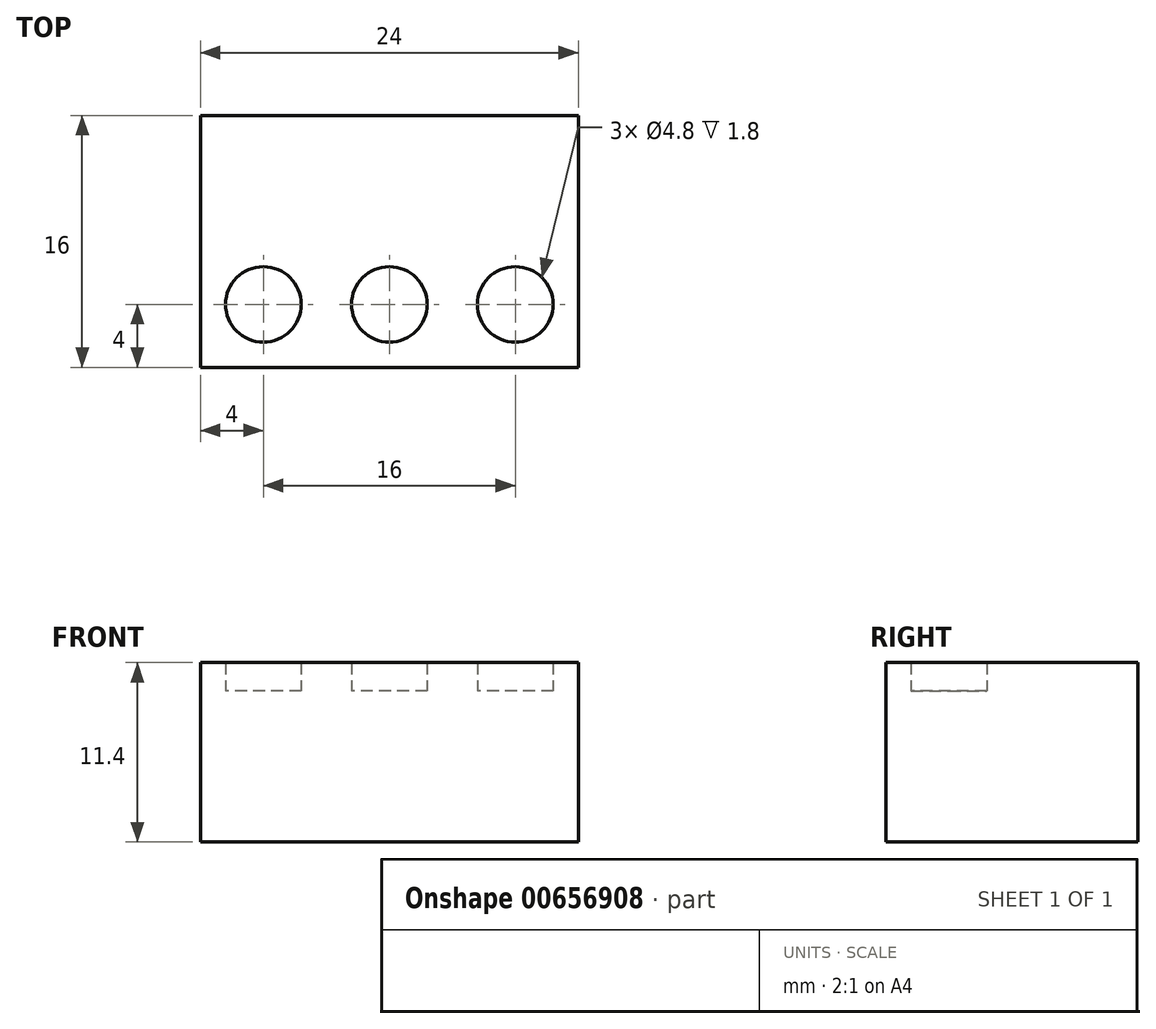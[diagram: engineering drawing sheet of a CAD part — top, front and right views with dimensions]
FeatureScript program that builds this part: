
annotation { "Feature Type Name" : "Feature", "Feature Type Description" : "" }
export const myFeature = defineFeature(function(context is Context, id is Id, definition is map)
    precondition{}
    {
        {
            var Q0;
            Q0=qCreatedBy(makeId("Top.planeOp"),FACE);
            var sketch = newSketch(context, id + "F0", { "sketchPlane" : qUnion([Q0])});
            skLineSegment(sketch, "E0.bottom", {"start": v(0, 0) * mm, "end": v(-24, 0) * mm});
            skLineSegment(sketch, "E0.top", {"start": v(0, 16) * mm, "end": v(-24, 16) * mm});
            skLineSegment(sketch, "E0.left", {"start": v(0, 0) * mm, "end": v(0, 16) * mm});
            skLineSegment(sketch, "E0.right", {"start": v(-24, 0) * mm, "end": v(-24, 16) * mm});
            skSolve(sketch);
        }
        {
            var Q0;
            Q0=makeQuery(id+"F0.imprint","IMPRINT",FACE,{"disambiguationData":[TD([[makeQuery(id+"F0.imprint","IMPRINT",EDGE,{"derivedFrom":sQuery(id+"F0.wireOp",EDGE,"E0.bottom")}),-1.0]])]});
            extrude(context, id + "F1", {"entities" : qUnion([Q0]), "depth" : 9.6 * mm, "offsetDistance" : 25.4 * mm});
        }
        {
            var Q0;
            Q0=makeQuery(id+"F1.opExtrude","CAP_FACE",FACE,{"disambiguationData":[OSD([sQuery(id+"F0.wireOp",EDGE,"E0.bottom"),sQuery(id+"F0.wireOp",EDGE,"E0.top"),sQuery(id+"F0.wireOp",EDGE,"E0.left"),sQuery(id+"F0.wireOp",EDGE,"E0.right")])],"isStart":false});
            var sketch = newSketch(context, id + "F2", { "sketchPlane" : qUnion([Q0])});
            skLineSegment(sketch, "E1", {"start": v(-24, 8) * mm, "end": v(0, 8) * mm, "construction": true});
            skLineSegment(sketch, "E2", {"start": v(-16, 16) * mm, "end": v(-16, 0) * mm});
            skLineSegment(sketch, "E3", {"start": v(-8, 16) * mm, "end": v(-8, 0) * mm});
            skLineSegment(sketch, "E4", {"start": v(-24, 16) * mm, "end": v(-16, 8) * mm, "construction": true});
            skLineSegment(sketch, "E5", {"start": v(-16, 8) * mm, "end": v(-8, 16) * mm, "construction": true});
            skLineSegment(sketch, "E6", {"start": v(-8, 16) * mm, "end": v(0, 8) * mm, "construction": true});
            skCircle(sketch, "E7", {"center": v(-20, 12) * mm, "radius": 2.4 * mm});
            skCircle(sketch, "E8", {"center": v(-12, 12) * mm, "radius": 2.4 * mm});
            skCircle(sketch, "E9", {"center": v(-4, 12) * mm, "radius": 2.4 * mm});
            skCircle(sketch, "E10.MirrorC", {"center": v(-20, 4) * mm, "radius": 2.4 * mm});
            skCircle(sketch, "E11.MirrorC", {"center": v(-12, 4) * mm, "radius": 2.4 * mm});
            skCircle(sketch, "E12.MirrorC", {"center": v(-4, 4) * mm, "radius": 2.4 * mm});
            skSolve(sketch);
        }
        {
            var Q0;
            Q0=makeQuery(id+"F2.imprint","IMPRINT",FACE,{"disambiguationData":[TD([[makeQuery(id+"F2.imprint","IMPRINT",EDGE,{"derivedFrom":sQuery(id+"F2.wireOp",EDGE,"E7")}),1.0]])]});
            var Q1;
            Q1=makeQuery(id+"F2.imprint","IMPRINT",FACE,{"disambiguationData":[TD([[makeQuery(id+"F2.imprint","IMPRINT",EDGE,{"derivedFrom":sQuery(id+"F2.wireOp",EDGE,"E8")}),1.0]])]});
            var Q2;
            Q2=makeQuery(id+"F2.imprint","IMPRINT",FACE,{"disambiguationData":[TD([[makeQuery(id+"F2.imprint","IMPRINT",EDGE,{"derivedFrom":sQuery(id+"F2.wireOp",EDGE,"E9")}),1.0]])]});
            var Q3;
            Q3=makeQuery(id+"F2.imprint","IMPRINT",FACE,{"disambiguationData":[TD([[makeQuery(id+"F2.imprint","IMPRINT",EDGE,{"derivedFrom":sQuery(id+"F2.wireOp",EDGE,"E10.MirrorC")}),-1.0]])]});
            var Q4;
            Q4=makeQuery(id+"F2.imprint","IMPRINT",FACE,{"disambiguationData":[TD([[makeQuery(id+"F2.imprint","IMPRINT",EDGE,{"derivedFrom":sQuery(id+"F2.wireOp",EDGE,"E11.MirrorC")}),-1.0]])]});
            var Q5;
            Q5=makeQuery(id+"F2.imprint","IMPRINT",FACE,{"disambiguationData":[TD([[makeQuery(id+"F2.imprint","IMPRINT",EDGE,{"derivedFrom":sQuery(id+"F2.wireOp",EDGE,"E12.MirrorC")}),-1.0]])]});
            extrude(context, id + "F3", {"entities" : qUnion([Q0, Q1, Q2, Q3, Q4, Q5]), "operationType" : NewBodyOperationType.ADD, "depth" : 1.8 * mm, "offsetDistance" : 25.4 * mm});
        }
    });
